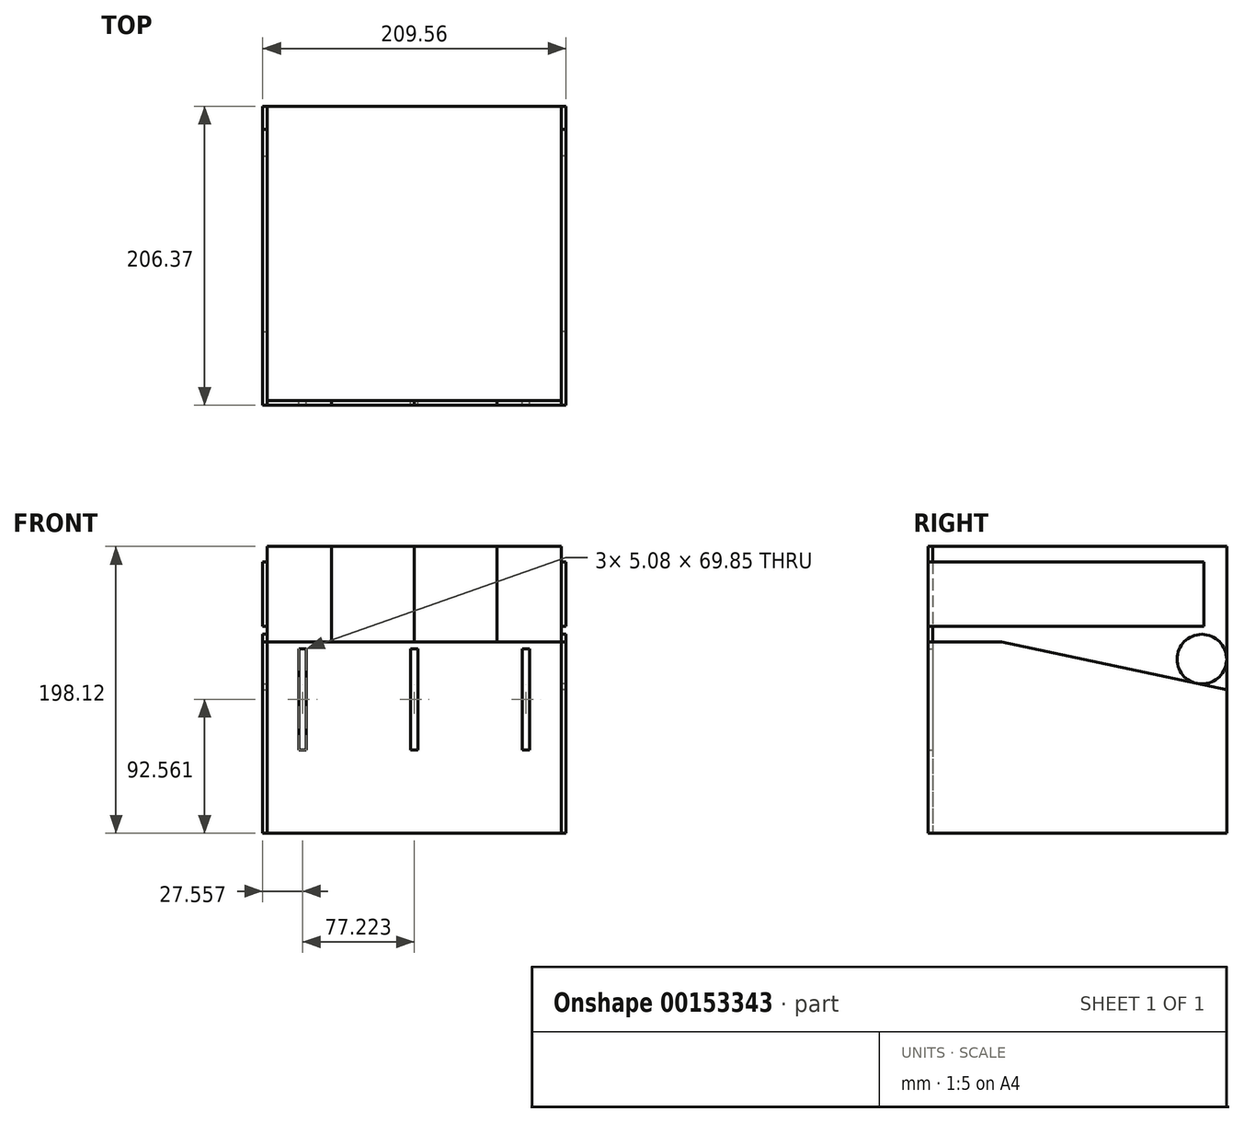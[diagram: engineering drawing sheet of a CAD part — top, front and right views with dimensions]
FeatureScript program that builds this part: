
annotation { "Feature Type Name" : "Feature", "Feature Type Description" : "" }
export const myFeature = defineFeature(function(context is Context, id is Id, definition is map)
    precondition{}
    {
        {
            var Q0;
            Q0=qCreatedBy(makeId("Top.planeOp"),FACE);
            var sketch = newSketch(context, id + "F0", { "sketchPlane" : qUnion([Q0])});
            skLineSegment(sketch, "E0.bottom", {"start": v(101.6, 101.6) * mm, "end": v(-101.6, 101.6) * mm});
            skLineSegment(sketch, "E0.top", {"start": v(101.6, -101.6) * mm, "end": v(-101.6, -101.6) * mm});
            skLineSegment(sketch, "E0.left", {"start": v(101.6, 101.6) * mm, "end": v(101.6, -101.6) * mm});
            skLineSegment(sketch, "E0.right", {"start": v(-101.6, 101.6) * mm, "end": v(-101.6, -101.6) * mm});
            skPoint(sketch, "E0.middle", {"position": v(0, 0) * mm});
            skSolve(sketch);
        }
        {
            var Q0;
            Q0=makeQuery(id+"F0.imprint","IMPRINT",FACE,{"disambiguationData":[TD([[makeQuery(id+"F0.imprint","IMPRINT",EDGE,{"derivedFrom":sQuery(id+"F0.wireOp",EDGE,"E0.bottom")}),1.0]])]});
            extrude(context, id + "F1", {"entities" : qUnion([Q0]), "depth" : 198.12 * mm});
        }
        {
            var Q0;
            Q0=makeQuery(id+"F1.opExtrude","SWEPT_FACE",FACE,{"disambiguationData":[OSD([sQuery(id+"F0.wireOp",EDGE,"E0.top")])]});
            var sketch = newSketch(context, id + "F2", { "sketchPlane" : qUnion([Q0])});
            skLineSegment(sketch, "E1.bottom", {"start": v(-101.6, 132.08) * mm, "end": v(101.6, 132.08) * mm});
            skLineSegment(sketch, "E1.top", {"start": v(-101.6, 0) * mm, "end": v(101.6, 0) * mm});
            skLineSegment(sketch, "E1.left", {"start": v(-101.6, 132.08) * mm, "end": v(-101.6, 0) * mm});
            skLineSegment(sketch, "E1.right", {"start": v(101.6, 132.08) * mm, "end": v(101.6, 0) * mm});
            skLineSegment(sketch, "E2", {"start": v(0, 132.08) * mm, "end": v(0, 0) * mm, "construction": true});
            skLineSegment(sketch, "E3.bottom", {"start": v(2.54, 127.49) * mm, "end": v(-2.54, 127.49) * mm});
            skLineSegment(sketch, "E3.top", {"start": v(2.54, 57.64) * mm, "end": v(-2.54, 57.64) * mm});
            skLineSegment(sketch, "E3.left", {"start": v(2.54, 127.49) * mm, "end": v(2.54, 57.64) * mm});
            skLineSegment(sketch, "E3.right", {"start": v(-2.54, 127.49) * mm, "end": v(-2.54, 57.64) * mm});
            skPoint(sketch, "E3.middle", {"position": v(0, 92.56) * mm});
            skLineSegment(sketch, "E4.bottom", {"start": v(-74.68, 127.49) * mm, "end": v(-79.76, 127.49) * mm});
            skLineSegment(sketch, "E4.top", {"start": v(-74.68, 57.64) * mm, "end": v(-79.76, 57.64) * mm});
            skLineSegment(sketch, "E4.left", {"start": v(-74.68, 127.49) * mm, "end": v(-74.68, 57.64) * mm});
            skLineSegment(sketch, "E4.right", {"start": v(-79.76, 127.49) * mm, "end": v(-79.76, 57.64) * mm});
            skPoint(sketch, "E4.middle", {"position": v(-77.22, 92.56) * mm});
            skLineSegment(sketch, "E5.MirrorCS", {"start": v(74.68, 57.64) * mm, "end": v(79.76, 57.64) * mm});
            skLineSegment(sketch, "E6.MirrorCS", {"start": v(74.68, 127.49) * mm, "end": v(79.76, 127.49) * mm});
            skPoint(sketch, "E7.MirrorP", {"position": v(77.22, 92.56) * mm});
            skLineSegment(sketch, "E8.MirrorCS", {"start": v(79.76, 127.49) * mm, "end": v(79.76, 57.64) * mm});
            skLineSegment(sketch, "E9.MirrorCS", {"start": v(74.68, 127.49) * mm, "end": v(74.68, 57.64) * mm});
            skSolve(sketch);
        }
        {
            var Q0;
            Q0=qSketchRegion(id+"F2",true);
            extrude(context, id + "F3", {"entities" : qUnion([Q0]), "depth" : 3.17 * mm});
        }
        {
            var Q0;
            Q0=makeQuery(id+"F1.opExtrude","SWEPT_FACE",FACE,{"disambiguationData":[OSD([sQuery(id+"F0.wireOp",EDGE,"E0.top")])]});
            var sketch = newSketch(context, id + "F4", { "sketchPlane" : qUnion([Q0])});
            skLineSegment(sketch, "E10.0", {"start": v(-101.6, 132.08) * mm, "end": v(101.6, 132.08) * mm, "construction": true});
            skLineSegment(sketch, "E11.bottom", {"start": v(-101.6, 132.08) * mm, "end": v(-57.15, 132.08) * mm});
            skLineSegment(sketch, "E11.top", {"start": v(-101.6, 198.12) * mm, "end": v(-57.15, 198.12) * mm});
            skLineSegment(sketch, "E11.left", {"start": v(-101.6, 132.08) * mm, "end": v(-101.6, 198.12) * mm});
            skLineSegment(sketch, "E11.right", {"start": v(-57.15, 132.08) * mm, "end": v(-57.15, 198.12) * mm});
            skLineSegment(sketch, "E12", {"start": v(0, 198.12) * mm, "end": v(0, 0) * mm, "construction": true});
            skLineSegment(sketch, "E13.MirrorCS", {"start": v(101.6, 132.08) * mm, "end": v(57.15, 132.08) * mm});
            skLineSegment(sketch, "E14.MirrorCS", {"start": v(101.6, 132.08) * mm, "end": v(101.6, 198.12) * mm});
            skLineSegment(sketch, "E15.MirrorCS", {"start": v(57.15, 132.08) * mm, "end": v(57.15, 198.12) * mm});
            skLineSegment(sketch, "E16.MirrorCS", {"start": v(101.6, 198.12) * mm, "end": v(57.15, 198.12) * mm});
            skSolve(sketch);
        }
        {
            var Q0;
            Q0=qSketchRegion(id+"F4",true);
            extrude(context, id + "F5", {"entities" : qUnion([Q0]), "depth" : 3.17 * mm});
        }
        {
            var Q0;
            Q0=makeQuery(id+"F1.opExtrude","SWEPT_FACE",FACE,{"disambiguationData":[OSD([sQuery(id+"F0.wireOp",EDGE,"E0.top")])]});
            var sketch = newSketch(context, id + "F6", { "sketchPlane" : qUnion([Q0])});
            skLineSegment(sketch, "E17.0", {"start": v(-101.6, 132.08) * mm, "end": v(101.6, 132.08) * mm, "construction": true});
            skLineSegment(sketch, "E18.bottom", {"start": v(0, 198.12) * mm, "end": v(57.15, 198.12) * mm});
            skLineSegment(sketch, "E18.top", {"start": v(0, 132.08) * mm, "end": v(57.15, 132.08) * mm});
            skLineSegment(sketch, "E18.left", {"start": v(0, 198.12) * mm, "end": v(0, 132.08) * mm});
            skLineSegment(sketch, "E18.right", {"start": v(57.15, 198.12) * mm, "end": v(57.15, 132.08) * mm});
            skSolve(sketch);
        }
        {
            var Q0;
            Q0=qSketchRegion(id+"F6",true);
            extrude(context, id + "F7", {"entities" : qUnion([Q0]), "depth" : 3.17 * mm});
        }
        {
            var Q0;
            Q0=makeQuery(id+"F1.opExtrude","SWEPT_FACE",FACE,{"disambiguationData":[OSD([sQuery(id+"F0.wireOp",EDGE,"E0.left")])]});
            var sketch = newSketch(context, id + "F8", { "sketchPlane" : qUnion([Q0])});
            skLineSegment(sketch, "E19.0", {"start": v(-104.78, 198.12) * mm, "end": v(-104.78, 132.08) * mm, "construction": true});
            skLineSegment(sketch, "E20.bottom", {"start": v(-104.78, 187.33) * mm, "end": v(85.72, 187.33) * mm});
            skLineSegment(sketch, "E20.top", {"start": v(-104.78, 142.88) * mm, "end": v(85.72, 142.88) * mm});
            skLineSegment(sketch, "E20.left", {"start": v(-104.78, 187.33) * mm, "end": v(-104.78, 142.88) * mm});
            skLineSegment(sketch, "E20.right", {"start": v(85.73, 187.33) * mm, "end": v(85.73, 142.88) * mm});
            skPoint(sketch, "E21", {"position": v(-104.78, 165.1) * mm});
            skSolve(sketch);
        }
        {
            var Q0;
            Q0=qSketchRegion(id+"F8",true);
            extrude(context, id + "F9", {"entities" : qUnion([Q0]), "depth" : 3.17 * mm});
        }
        {
            var Q0;
            Q0=makeQuery(id+"F1.opExtrude","SWEPT_FACE",FACE,{"disambiguationData":[OSD([sQuery(id+"F0.wireOp",EDGE,"E0.left")])]});
            var sketch = newSketch(context, id + "F10", { "sketchPlane" : qUnion([Q0])});
            skLineSegment(sketch, "E22.0", {"start": v(-104.78, 132.08) * mm, "end": v(-104.78, 0) * mm, "construction": true});
            skLineSegment(sketch, "E23", {"start": v(-104.78, 132.08) * mm, "end": v(-53.98, 132.08) * mm});
            skLineSegment(sketch, "E24", {"start": v(-53.98, 132.08) * mm, "end": v(101.6, 99.06) * mm});
            skLineSegment(sketch, "E25", {"start": v(101.6, 99.06) * mm, "end": v(101.6, 0) * mm});
            skLineSegment(sketch, "E26", {"start": v(101.6, 0) * mm, "end": v(-104.78, 0) * mm});
            skLineSegment(sketch, "E27", {"start": v(-104.78, 132.08) * mm, "end": v(-104.78, 0) * mm});
            skSolve(sketch);
        }
        {
            var Q0;
            Q0=qSketchRegion(id+"F10",true);
            extrude(context, id + "F11", {"entities" : qUnion([Q0]), "depth" : 3.17 * mm});
        }
        {
            var Q0;
            Q0=makeQuery(id+"F11.opExtrude","SWEPT_BODY",BODY,{"disambiguationData":[OSD([sQuery(id+"F10.wireOp",EDGE,"E23"),sQuery(id+"F10.wireOp",EDGE,"E24"),sQuery(id+"F10.wireOp",EDGE,"E25"),sQuery(id+"F10.wireOp",EDGE,"E26"),sQuery(id+"F10.wireOp",EDGE,"E27")])]});
            var Q1;
            Q1=makeQuery(id+"F9.opExtrude","SWEPT_BODY",BODY,{"disambiguationData":[OSD([sQuery(id+"F8.wireOp",EDGE,"E20.bottom"),sQuery(id+"F8.wireOp",EDGE,"E20.top"),sQuery(id+"F8.wireOp",EDGE,"E20.left"),sQuery(id+"F8.wireOp",EDGE,"E20.right")])]});
            var Q2;
            Q2=makeQuery(id+"F7.opExtrude","SWEPT_FACE",FACE,{"disambiguationData":[OSD([sQuery(id+"F6.wireOp",EDGE,"E18.left")])]});
            mirror(context, id + "F12", {"entities" : qUnion([Q0, Q1]), "mirrorPlane" : qUnion([Q2])});
        }
        {
            var Q0;
            Q0=makeQuery(id+"F1.opExtrude","SWEPT_FACE",FACE,{"disambiguationData":[OSD([sQuery(id+"F0.wireOp",EDGE,"E0.left")])]});
            var sketch = newSketch(context, id + "F13", { "sketchPlane" : qUnion([Q0])});
            skCircle(sketch, "E28", {"center": v(84.46, 120.23) * mm, "radius": 17.15 * mm});
            skSolve(sketch);
        }
        {
            var Q0;
            Q0 = qSketchRegion(id + "F13", true);
            extrude(context, id + "F14", {"entities" : qUnion([Q0]), "depth" : 3.17 * mm});
        }
        {
            var Q0;
            Q0=makeQuery(id+"F1.opExtrude","SWEPT_FACE",FACE,{"disambiguationData":[OSD([sQuery(id+"F0.wireOp",EDGE,"E0.right")])]});
            var sketch = newSketch(context, id + "F15", { "sketchPlane" : qUnion([Q0])});
            skCircle(sketch, "E29", {"center": v(-84.46, 120.23) * mm, "radius": 17.15 * mm});
            skSolve(sketch);
        }
        {
            var Q0;
            Q0 = qSketchRegion(id + "F15", true);
            extrude(context, id + "F16", {"entities" : qUnion([Q0]), "depth" : 3.17 * mm});
        }
    });
